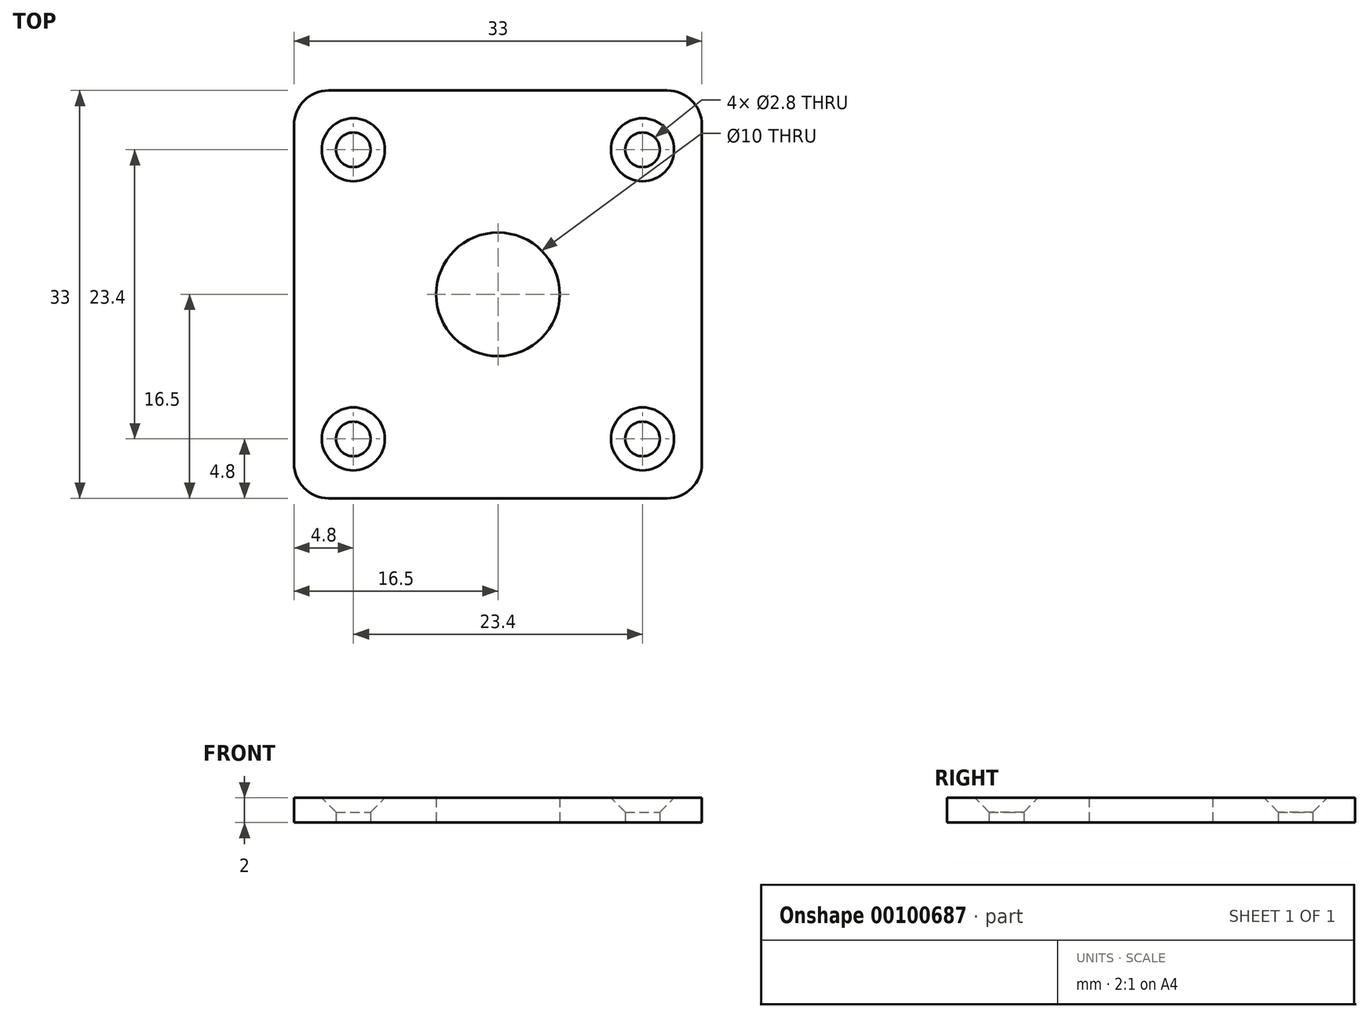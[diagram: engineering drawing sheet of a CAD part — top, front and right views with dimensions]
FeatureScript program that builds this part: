
annotation { "Feature Type Name" : "Feature", "Feature Type Description" : "" }
export const myFeature = defineFeature(function(context is Context, id is Id, definition is map)
    precondition{}
    {
        {
            var Q0;
            Q0=qCreatedBy(makeId("Top.planeOp"),FACE);
            var sketch = newSketch(context, id + "F0", { "sketchPlane" : qUnion([Q0])});
            skLineSegment(sketch, "E0.bottom", {"start": v(16.5, -16.5) * mm, "end": v(-16.5, -16.5) * mm});
            skLineSegment(sketch, "E0.top", {"start": v(16.5, 16.5) * mm, "end": v(-16.5, 16.5) * mm});
            skLineSegment(sketch, "E0.left", {"start": v(16.5, -16.5) * mm, "end": v(16.5, 16.5) * mm});
            skLineSegment(sketch, "E0.right", {"start": v(-16.5, -16.5) * mm, "end": v(-16.5, 16.5) * mm});
            skPoint(sketch, "E0.middle", {"position": v(0, 0) * mm});
            skSolve(sketch);
        }
        {
            var Q0;
            Q0 = qSketchRegion(id + "F0", true);
            extrude(context, id + "F1", {"entities" : qUnion([Q0]), "depth" : 2 * mm});
        }
        {
            var Q0;
            Q0=makeQuery(id+"F1.opExtrude","CAP_FACE",FACE,{"disambiguationData":[OSD([sQuery(id+"F0.wireOp",EDGE,"E0.bottom"),sQuery(id+"F0.wireOp",EDGE,"E0.top"),sQuery(id+"F0.wireOp",EDGE,"E0.left"),sQuery(id+"F0.wireOp",EDGE,"E0.right")])],"isStart":false});
            var sketch = newSketch(context, id + "F2", { "sketchPlane" : qUnion([Q0])});
            skPoint(sketch, "E1", {"position": v(0, 0) * mm});
            skSolve(sketch);
        }
        {
            var Q0;
            Q0=sQuery(id+"F2.wireOp",VERTEX,"E1");
            var Q1;
            Q1=makeQuery(id+"F1.opExtrude","SWEPT_BODY",BODY,{"disambiguationData":[OSD([sQuery(id+"F0.wireOp",EDGE,"E0.bottom"),sQuery(id+"F0.wireOp",EDGE,"E0.top"),sQuery(id+"F0.wireOp",EDGE,"E0.left"),sQuery(id+"F0.wireOp",EDGE,"E0.right")])]});
            hole(context, id + "F3", {"style" : HoleStyle.SIMPLE, "endStyle" : HoleEndStyle.THROUGH, "holeDiameter" : 10 * mm, "locations" : qUnion([Q0]), "scope" : qUnion([Q1]), "isTappedThrough" : true, "startStyle" : HoleStartStyle.PART});
        }
        {
            var Q0;
            Q0=makeQuery(id+"F1.opExtrude","CAP_FACE",FACE,{"disambiguationData":[OSD([sQuery(id+"F0.wireOp",EDGE,"E0.bottom"),sQuery(id+"F0.wireOp",EDGE,"E0.top"),sQuery(id+"F0.wireOp",EDGE,"E0.left"),sQuery(id+"F0.wireOp",EDGE,"E0.right")])],"isStart":false});
            var sketch = newSketch(context, id + "F4", { "sketchPlane" : qUnion([Q0])});
            skPoint(sketch, "E2", {"position": v(11.7, -11.7) * mm});
            skPoint(sketch, "E3", {"position": v(11.7, 11.7) * mm});
            skLineSegment(sketch, "E4", {"start": v(11.7, 11.7) * mm, "end": v(11.7, -11.7) * mm, "construction": true});
            skPoint(sketch, "E5.MirrorP", {"position": v(-11.7, 11.7) * mm});
            skPoint(sketch, "E6.MirrorP", {"position": v(-11.7, -11.7) * mm});
            skSolve(sketch);
        }
        {
            var Q0;
            Q0=sQuery(id+"F4.wireOp",VERTEX,"E6.MirrorP");
            var Q1;
            Q1=sQuery(id+"F4.wireOp",VERTEX,"E2");
            var Q2;
            Q2=sQuery(id+"F4.wireOp",VERTEX,"E3");
            var Q3;
            Q3=sQuery(id+"F4.wireOp",VERTEX,"E5.MirrorP");
            var Q4;
            Q4=makeQuery(id+"F1.opExtrude","SWEPT_BODY",BODY,{"disambiguationData":[OSD([sQuery(id+"F0.wireOp",EDGE,"E0.bottom"),sQuery(id+"F0.wireOp",EDGE,"E0.top"),sQuery(id+"F0.wireOp",EDGE,"E0.left"),sQuery(id+"F0.wireOp",EDGE,"E0.right")])]});
            hole(context, id + "F5", {"style" : HoleStyle.C_SINK, "endStyle" : HoleEndStyle.THROUGH, "holeDiameter" : 2.8 * mm, "cSinkDiameter" : 5.1 * mm, "cSinkAngle" : 90 * degree, "locations" : qUnion([Q0, Q1, Q2, Q3]), "scope" : qUnion([Q4]), "isTappedThrough" : true, "startStyle" : HoleStartStyle.PART});
        }
        {
            var Q0;
            Q0=makeQuery(id+"F1.opExtrude","SWEPT_EDGE",EDGE,{"disambiguationData":[OSD([sQuery(id+"F0.wireOp",EDGE,"E0.bottom"),sQuery(id+"F0.wireOp",EDGE,"E0.right")])]});
            var Q1;
            Q1=makeQuery(id+"F1.opExtrude","SWEPT_EDGE",EDGE,{"disambiguationData":[OSD([sQuery(id+"F0.wireOp",EDGE,"E0.bottom"),sQuery(id+"F0.wireOp",EDGE,"E0.left")])]});
            var Q2;
            Q2=makeQuery(id+"F1.opExtrude","SWEPT_EDGE",EDGE,{"disambiguationData":[OSD([sQuery(id+"F0.wireOp",EDGE,"E0.top"),sQuery(id+"F0.wireOp",EDGE,"E0.left")])]});
            var Q3;
            Q3=makeQuery(id+"F1.opExtrude","SWEPT_EDGE",EDGE,{"disambiguationData":[OSD([sQuery(id+"F0.wireOp",EDGE,"E0.top"),sQuery(id+"F0.wireOp",EDGE,"E0.right")])]});
            fillet(context, id + "F6", {"entities" : qUnion([Q0, Q1, Q2, Q3]), "radius" : 2.8 * mm, "tangentPropagation" : true, "allowEdgeOverflow" : false});
        }
    });
